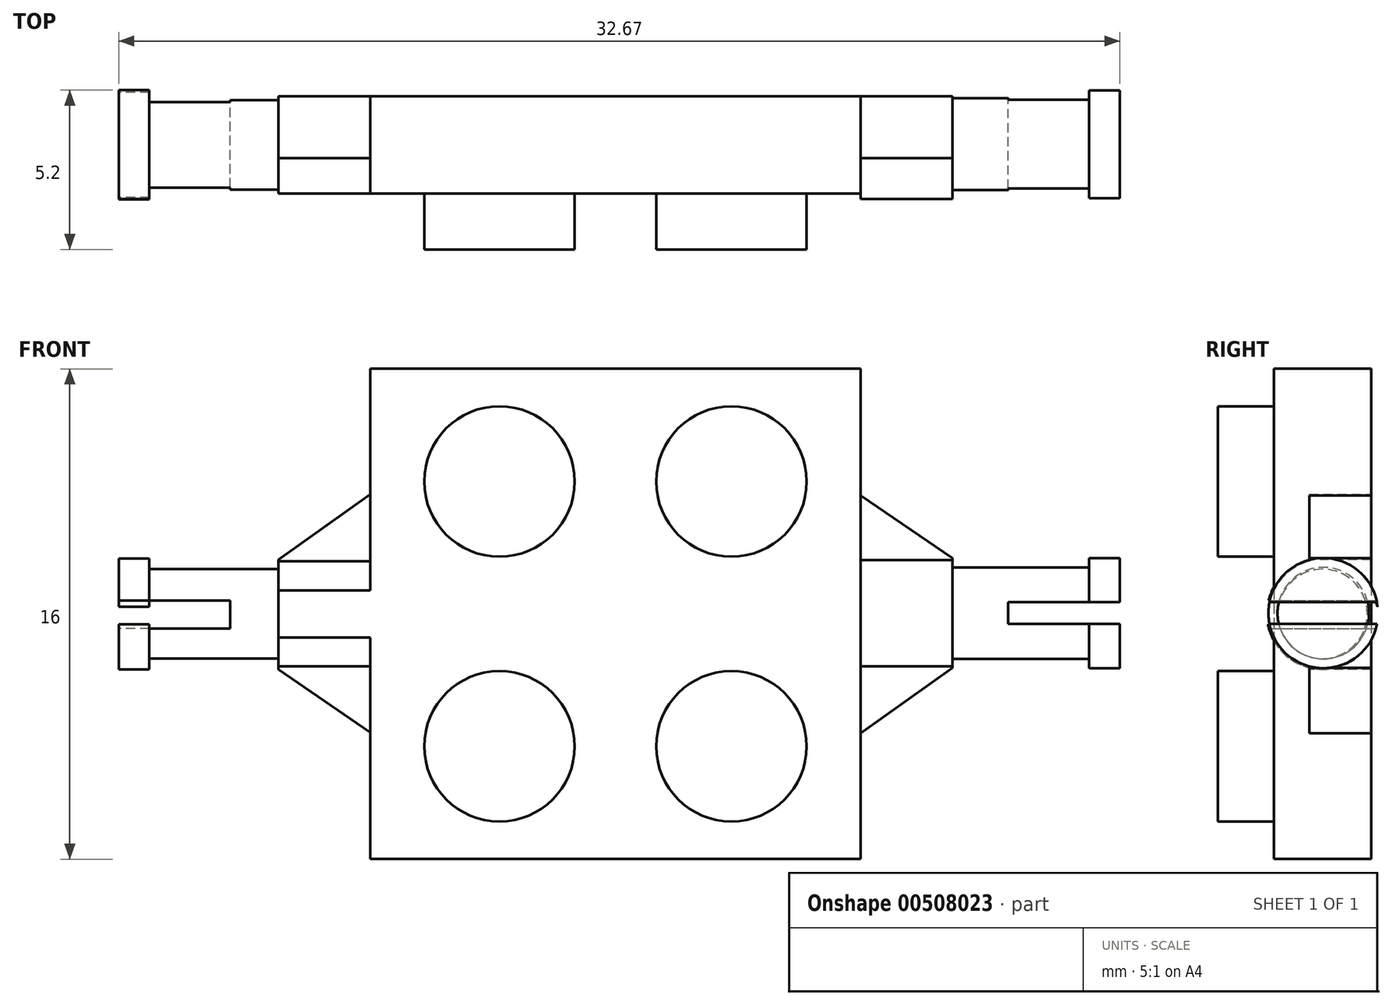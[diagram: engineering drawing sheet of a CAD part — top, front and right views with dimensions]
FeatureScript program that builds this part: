
annotation { "Feature Type Name" : "Feature", "Feature Type Description" : "" }
export const myFeature = defineFeature(function(context is Context, id is Id, definition is map)
    precondition{}
    {
        {
            var Q0;
            Q0=qCreatedBy(makeId("Front.planeOp"),FACE);
            var sketch = newSketch(context, id + "F0", { "sketchPlane" : qUnion([Q0])});
            skLineSegment(sketch, "E0.bottom", {"start": v(-45.17, 38.26) * mm, "end": v(-29.17, 38.26) * mm});
            skLineSegment(sketch, "E0.top", {"start": v(-45.17, 22.26) * mm, "end": v(-29.17, 22.26) * mm});
            skLineSegment(sketch, "E0.left", {"start": v(-45.17, 38.26) * mm, "end": v(-45.17, 22.26) * mm});
            skLineSegment(sketch, "E0.right", {"start": v(-29.17, 38.26) * mm, "end": v(-29.17, 22.26) * mm});
            skSolve(sketch);
        }
        {
            var Q0;
            Q0 = qSketchRegion(id + "F0", true);
            extrude(context, id + "F1", {"entities" : qUnion([Q0]), "depth" : 3.18 * mm});
        }
        {
            var Q0;
            Q0=makeQuery(id+"F1.opExtrude","CAP_FACE",FACE,{"disambiguationData":[OSD([sQuery(id+"F0.wireOp",EDGE,"E0.bottom"),sQuery(id+"F0.wireOp",EDGE,"E0.top"),sQuery(id+"F0.wireOp",EDGE,"E0.left"),sQuery(id+"F0.wireOp",EDGE,"E0.right")])],"isStart":false});
            var sketch = newSketch(context, id + "F2", { "sketchPlane" : qUnion([Q0])});
            skCircle(sketch, "E1", {"center": v(-40.96, 34.59) * mm, "radius": 2.46 * mm});
            skCircle(sketch, "E2", {"center": v(-33.39, 34.59) * mm, "radius": 2.46 * mm});
            skCircle(sketch, "E3", {"center": v(-33.39, 25.94) * mm, "radius": 2.46 * mm});
            skCircle(sketch, "E4", {"center": v(-40.96, 25.94) * mm, "radius": 2.46 * mm});
            skSolve(sketch);
        }
        {
            var Q0;
            Q0=makeQuery(id+"F2.imprint","IMPRINT",FACE,{"disambiguationData":[TD([[makeQuery(id+"F2.imprint","IMPRINT",EDGE,{"derivedFrom":sQuery(id+"F2.wireOp",EDGE,"E4")}),1.0]])]});
            var Q1;
            Q1=makeQuery(id+"F2.imprint","IMPRINT",FACE,{"disambiguationData":[TD([[makeQuery(id+"F2.imprint","IMPRINT",EDGE,{"derivedFrom":sQuery(id+"F2.wireOp",EDGE,"E3")}),1.0]])]});
            var Q2;
            Q2=makeQuery(id+"F2.imprint","IMPRINT",FACE,{"disambiguationData":[TD([[makeQuery(id+"F2.imprint","IMPRINT",EDGE,{"derivedFrom":sQuery(id+"F2.wireOp",EDGE,"E2")}),1.0]])]});
            var Q3;
            Q3=makeQuery(id+"F2.imprint","IMPRINT",FACE,{"disambiguationData":[TD([[makeQuery(id+"F2.imprint","IMPRINT",EDGE,{"derivedFrom":sQuery(id+"F2.wireOp",EDGE,"E1")}),1.0]])]});
            extrude(context, id + "F3", {"entities" : qUnion([Q0, Q1, Q2, Q3]), "operationType" : NewBodyOperationType.ADD, "depth" : 1.82 * mm});
        }
        {
            var Q0;
            Q0=makeQuery(id+"F1.opExtrude","SWEPT_FACE",FACE,{"disambiguationData":[OSD([sQuery(id+"F0.wireOp",EDGE,"E0.left")])]});
            var sketch = newSketch(context, id + "F4", { "sketchPlane" : qUnion([Q0])});
            skLineSegment(sketch, "E5.bottom", {"start": v(2.02, 34.16) * mm, "end": v(0, 34.16) * mm});
            skLineSegment(sketch, "E5.top", {"start": v(2.02, 26.4) * mm, "end": v(0, 26.4) * mm});
            skLineSegment(sketch, "E5.left", {"start": v(2.02, 34.16) * mm, "end": v(2.02, 26.4) * mm});
            skLineSegment(sketch, "E5.right", {"start": v(0, 34.16) * mm, "end": v(0, 26.4) * mm});
            skSolve(sketch);
        }
        {
            var Q0;
            Q0=makeQuery(id+"F4.imprint","IMPRINT",FACE,{"disambiguationData":[TD([[makeQuery(id+"F4.imprint","IMPRINT",EDGE,{"derivedFrom":sQuery(id+"F4.wireOp",EDGE,"E5.bottom")}),1.0]])]});
            extrude(context, id + "F5", {"entities" : qUnion([Q0]), "operationType" : NewBodyOperationType.ADD, "depth" : 3 * mm});
        }
        {
            var Q0;
            Q0=makeQuery(id+"F5.opExtrude","SWEPT_FACE",FACE,{"disambiguationData":[OSD([sQuery(id+"F4.wireOp",EDGE,"E5.left")])]});
            var sketch = newSketch(context, id + "F6", { "sketchPlane" : qUnion([Q0])});
            skLineSegment(sketch, "E6", {"start": v(-45.17, 26.4) * mm, "end": v(-48.17, 28.45) * mm});
            skLineSegment(sketch, "E7", {"start": v(-45.17, 34.16) * mm, "end": v(-48.17, 32.03) * mm});
            skLineSegment(sketch, "E8", {"start": v(-45.17, 34.16) * mm, "end": v(-48.17, 34.16) * mm});
            skLineSegment(sketch, "E9", {"start": v(-48.17, 34.16) * mm, "end": v(-48.17, 32.03) * mm});
            skLineSegment(sketch, "E10", {"start": v(-45.17, 26.4) * mm, "end": v(-48.17, 26.4) * mm});
            skLineSegment(sketch, "E11", {"start": v(-48.17, 26.4) * mm, "end": v(-48.17, 28.45) * mm});
            skSolve(sketch);
        }
        {
            var Q0;
            Q0=makeQuery(id+"F6.imprint","IMPRINT",FACE,{"disambiguationData":[TD([[makeQuery(id+"F6.imprint","IMPRINT",EDGE,{"derivedFrom":sQuery(id+"F6.wireOp",EDGE,"E7")}),-1.0]])]});
            var Q1;
            Q1=makeQuery(id+"F6.imprint","IMPRINT",FACE,{"disambiguationData":[TD([[makeQuery(id+"F6.imprint","IMPRINT",EDGE,{"derivedFrom":sQuery(id+"F6.wireOp",EDGE,"E6")}),1.0]])]});
            extrude(context, id + "F7", {"entities" : qUnion([Q0, Q1]), "operationType" : NewBodyOperationType.REMOVE, "oppositeDirection" : true, "depth" : 25 * mm});
        }
        {
            var Q0;
            Q0=makeQuery(id+"F1.opExtrude","SWEPT_FACE",FACE,{"disambiguationData":[OSD([sQuery(id+"F0.wireOp",EDGE,"E0.left")])]});
            var sketch = newSketch(context, id + "F8", { "sketchPlane" : qUnion([Q0])});
            skCircle(sketch, "E12", {"center": v(1.6, 30.26) * mm, "radius": 1.77 * mm});
            skPoint(sketch, "E12.centerSnap0", {"position": v(1.6, 38.26) * mm});
            skPoint(sketch, "E12.centerSnap1", {"position": v(3.18, 30.26) * mm});
            skSolve(sketch);
        }
        {
            var Q0;
            {var subQ0=sQuery(id+"F8.wireOp",EDGE,"E12");var subQ1=makeQuery(id+"F5.opExtrude","CAP_EDGE",EDGE,{"disambiguationData":[OSD([sQuery(id+"F4.wireOp",EDGE,"E5.left")])],"isStart":true});var subQ2=makeQuery(id+"F8.imprint","INTERSECT",VERTEX,{"disambiguationData":[OD(0.0)],"derivedFrom":[subQ1,subQ0]});Q0=makeQuery(id+"F8.imprint","IMPRINT",FACE,{"disambiguationData":[TD([[makeQuery(id+"F8.imprint","IMPRINT",EDGE,{"disambiguationData":[TD([[subQ2,1.0]])],"derivedFrom":subQ0}),1.0]])]});}
            var Q1;
            {var subQ0=sQuery(id+"F8.wireOp",EDGE,"E12");var subQ1=makeQuery(id+"F1.opExtrude","CAP_EDGE",EDGE,{"disambiguationData":[OSD([sQuery(id+"F0.wireOp",EDGE,"E0.left")])],"isStart":false});var subQ2=makeQuery(id+"F8.imprint","INTERSECT",VERTEX,{"disambiguationData":[OD(0.0)],"derivedFrom":[subQ1,subQ0]});Q1=makeQuery(id+"F8.imprint","IMPRINT",FACE,{"disambiguationData":[TD([[makeQuery(id+"F8.imprint","IMPRINT",EDGE,{"disambiguationData":[TD([[subQ2,1.0]])],"derivedFrom":subQ0}),1.0]])]});}
            extrude(context, id + "F9", {"entities" : qUnion([Q0, Q1]), "operationType" : NewBodyOperationType.ADD, "depth" : 3 * mm});
        }
        {
            var Q0;
            {var subQ0=sQuery(id+"F4.wireOp",EDGE,"E5.left");Q0=makeQuery(id+"F9.boolean.opBoolean","MERGE",FACE,{"derivedFrom":[makeQuery(id+"F5.opExtrude","CAP_FACE",FACE,{"disambiguationData":[OSD([sQuery(id+"F4.wireOp",EDGE,"E5.bottom"),sQuery(id+"F4.wireOp",EDGE,"E5.top"),subQ0,sQuery(id+"F4.wireOp",EDGE,"E5.right")])],"isStart":false}),makeQuery(id+"F9.opExtrude","CAP_FACE",FACE,{"disambiguationData":[OSD([subQ0,sQuery(id+"F8.wireOp",EDGE,"E12")])],"isStart":false})]});}
            var sketch = newSketch(context, id + "F10", { "sketchPlane" : qUnion([Q0])});
            skCircle(sketch, "E13", {"center": v(1.6, 30.26) * mm, "radius": 1.46 * mm});
            skSolve(sketch);
        }
        {
            var Q0;
            Q0=makeQuery(id+"F10.imprint","IMPRINT",FACE,{"disambiguationData":[TD([[makeQuery(id+"F10.imprint","IMPRINT",EDGE,{"derivedFrom":sQuery(id+"F10.wireOp",EDGE,"E13")}),1.0]])]});
            extrude(context, id + "F11", {"entities" : qUnion([Q0]), "operationType" : NewBodyOperationType.ADD, "depth" : 5.2 * mm});
        }
        {
            var Q0;
            Q0=makeQuery(id+"F11.opExtrude","CAP_FACE",FACE,{"disambiguationData":[OSD([sQuery(id+"F10.wireOp",EDGE,"E13")])],"isStart":false});
            var sketch = newSketch(context, id + "F12", { "sketchPlane" : qUnion([Q0])});
            skCircle(sketch, "E14", {"center": v(1.6, 30.26) * mm, "radius": 1.81 * mm});
            skSolve(sketch);
        }
        {
            var Q0;
            Q0=makeQuery(id+"F12.imprint","IMPRINT",FACE,{"disambiguationData":[TD([[makeQuery(id+"F12.imprint","IMPRINT",EDGE,{"derivedFrom":sQuery(id+"F12.wireOp",EDGE,"E14")}),1.0]])]});
            extrude(context, id + "F13", {"entities" : qUnion([Q0]), "operationType" : NewBodyOperationType.ADD, "oppositeDirection" : true, "depth" : 1 * mm});
        }
        {
            var Q0;
            {var subQ0=sQuery(id+"F10.wireOp",EDGE,"E13");Q0=makeQuery(id+"F13.boolean.opBoolean","MERGE",FACE,{"derivedFrom":[makeQuery(id+"F11.opExtrude","CAP_FACE",FACE,{"disambiguationData":[OSD([subQ0])],"isStart":false}),makeQuery(id+"F13.opExtrude","CAP_FACE",FACE,{"disambiguationData":[OSD([subQ0,sQuery(id+"F12.wireOp",EDGE,"E14")])],"isStart":true})]});}
            var sketch = newSketch(context, id + "F14", { "sketchPlane" : qUnion([Q0])});
            skLineSegment(sketch, "E15.bottom", {"start": v(3.35, 30.7) * mm, "end": v(-0.13, 30.7) * mm});
            skLineSegment(sketch, "E15.top", {"start": v(3.3, 29.78) * mm, "end": v(-0.16, 29.78) * mm});
            skArc(sketch, "E16", {"start": v(3.3, 29.78) * mm, "mid": v(3.43, 30.24) * mm, "end": v(3.35, 30.7) * mm});
            skArc(sketch, "E17", {"start": v(-0.13, 30.7) * mm, "mid": v(-0.25, 30.24) * mm, "end": v(-0.16, 29.78) * mm});
            skSolve(sketch);
        }
        {
            var Q0;
            {var subQ1=sQuery(id+"F14.wireOp",EDGE,"E15.bottom");Q0=makeQuery(id+"F14.imprint","IMPRINT",FACE,{"disambiguationData":[TD([[makeQuery(id+"F14.imprint","IMPRINT",EDGE,{"derivedFrom":subQ1}),1.0]])]});}
            extrude(context, id + "F15", {"entities" : qUnion([Q0]), "operationType" : NewBodyOperationType.REMOVE, "oppositeDirection" : true, "depth" : 3.64 * mm});
        }
        {
            var Q0;
            Q0=makeQuery(id+"F1.opExtrude","SWEPT_FACE",FACE,{"disambiguationData":[OSD([sQuery(id+"F0.wireOp",EDGE,"E0.right")])]});
            var sketch = newSketch(context, id + "F16", { "sketchPlane" : qUnion([Q0])});
            skLineSegment(sketch, "E18.bottom", {"start": v(-2.02, 26.36) * mm, "end": v(0, 26.36) * mm});
            skLineSegment(sketch, "E18.top", {"start": v(-2.02, 34.13) * mm, "end": v(0, 34.13) * mm});
            skLineSegment(sketch, "E18.left", {"start": v(-2.02, 26.36) * mm, "end": v(-2.02, 34.13) * mm});
            skLineSegment(sketch, "E18.right", {"start": v(0, 26.36) * mm, "end": v(0, 34.13) * mm});
            skSolve(sketch);
        }
        {
            var Q0;
            Q0=makeQuery(id+"F16.imprint","IMPRINT",FACE,{"disambiguationData":[TD([[makeQuery(id+"F16.imprint","IMPRINT",EDGE,{"derivedFrom":sQuery(id+"F16.wireOp",EDGE,"E18.bottom")}),1.0]])]});
            extrude(context, id + "F17", {"entities" : qUnion([Q0]), "operationType" : NewBodyOperationType.ADD, "depth" : 3 * mm});
        }
        {
            var Q0;
            Q0=makeQuery(id+"F17.opExtrude","SWEPT_FACE",FACE,{"disambiguationData":[OSD([sQuery(id+"F16.wireOp",EDGE,"E18.left")])]});
            var sketch = newSketch(context, id + "F18", { "sketchPlane" : qUnion([Q0])});
            skLineSegment(sketch, "E19", {"start": v(-29.17, 34.13) * mm, "end": v(-26.17, 32.08) * mm});
            skLineSegment(sketch, "E20", {"start": v(-26.17, 32.08) * mm, "end": v(-26.17, 34.13) * mm});
            skLineSegment(sketch, "E21", {"start": v(-26.17, 34.13) * mm, "end": v(-29.17, 34.13) * mm});
            skLineSegment(sketch, "E22", {"start": v(-29.17, 26.36) * mm, "end": v(-26.17, 28.5) * mm});
            skLineSegment(sketch, "E23", {"start": v(-26.17, 28.5) * mm, "end": v(-26.17, 26.36) * mm});
            skLineSegment(sketch, "E24", {"start": v(-26.17, 26.36) * mm, "end": v(-29.17, 26.36) * mm});
            skSolve(sketch);
        }
        {
            var Q0;
            Q0=makeQuery(id+"F18.imprint","IMPRINT",FACE,{"disambiguationData":[TD([[makeQuery(id+"F18.imprint","IMPRINT",EDGE,{"derivedFrom":sQuery(id+"F18.wireOp",EDGE,"E22")}),-1.0]])]});
            var Q1;
            Q1=makeQuery(id+"F18.imprint","IMPRINT",FACE,{"disambiguationData":[TD([[makeQuery(id+"F18.imprint","IMPRINT",EDGE,{"derivedFrom":sQuery(id+"F18.wireOp",EDGE,"E19")}),1.0]])]});
            extrude(context, id + "F19", {"entities" : qUnion([Q0, Q1]), "operationType" : NewBodyOperationType.REMOVE, "oppositeDirection" : true, "depth" : 25 * mm});
        }
        {
            var Q0;
            Q0=makeQuery(id+"F17.opExtrude","CAP_FACE",FACE,{"disambiguationData":[OSD([sQuery(id+"F16.wireOp",EDGE,"E18.bottom"),sQuery(id+"F16.wireOp",EDGE,"E18.top"),sQuery(id+"F16.wireOp",EDGE,"E18.left"),sQuery(id+"F16.wireOp",EDGE,"E18.right")])],"isStart":false});
            var sketch = newSketch(context, id + "F20", { "sketchPlane" : qUnion([Q0])});
            skCircle(sketch, "E25", {"center": v(-1.56, 30.3) * mm, "radius": 1.79 * mm});
            skPoint(sketch, "E25.centerSnap0", {"position": v(-2.02, 30.3) * mm});
            skSolve(sketch);
        }
        {
            var Q0;
            {var subQ0=sQuery(id+"F20.wireOp",EDGE,"E25");var subQ1=sQuery(id+"F16.wireOp",EDGE,"E18.left");var subQ6=makeQuery(id+"F17.opExtrude","CAP_EDGE",EDGE,{"disambiguationData":[OSD([subQ1])],"isStart":false});var subQ9=makeQuery(id+"F20.imprint","INTERSECT",VERTEX,{"disambiguationData":[OD(0.0)],"derivedFrom":[subQ6,subQ0]});Q0=makeQuery(id+"F20.imprint","IMPRINT",FACE,{"disambiguationData":[TD([[makeQuery(id+"F20.imprint","IMPRINT",EDGE,{"disambiguationData":[TD([[subQ9,1.0]])],"derivedFrom":subQ6}),-1.0]])]});}
            var Q1;
            {var subQ0=sQuery(id+"F20.wireOp",EDGE,"E25");var subQ1=makeQuery(id+"F17.opExtrude","CAP_EDGE",EDGE,{"disambiguationData":[OSD([sQuery(id+"F16.wireOp",EDGE,"E18.left")])],"isStart":false});var subQ2=makeQuery(id+"F20.imprint","INTERSECT",VERTEX,{"disambiguationData":[OD(0.0)],"derivedFrom":[subQ1,subQ0]});Q1=makeQuery(id+"F20.imprint","IMPRINT",FACE,{"disambiguationData":[TD([[makeQuery(id+"F20.imprint","IMPRINT",EDGE,{"disambiguationData":[TD([[subQ2,-1.0]])],"derivedFrom":subQ0}),1.0]])]});}
            var Q2;
            {var subQ0=sQuery(id+"F20.wireOp",EDGE,"E25");var subQ1=makeQuery(id+"F17.opExtrude","CAP_EDGE",EDGE,{"disambiguationData":[OSD([sQuery(id+"F16.wireOp",EDGE,"E18.right")])],"isStart":false});var subQ2=makeQuery(id+"F20.imprint","INTERSECT",VERTEX,{"disambiguationData":[OD(0.0)],"derivedFrom":[subQ1,subQ0]});Q2=makeQuery(id+"F20.imprint","IMPRINT",FACE,{"disambiguationData":[TD([[makeQuery(id+"F20.imprint","IMPRINT",EDGE,{"disambiguationData":[TD([[subQ2,1.0]])],"derivedFrom":subQ0}),1.0]])]});}
            extrude(context, id + "F21", {"entities" : qUnion([Q0, Q1, Q2]), "operationType" : NewBodyOperationType.ADD, "oppositeDirection" : true, "depth" : 3 * mm});
        }
        {
            var Q0;
            Q0=makeQuery(id+"F21.boolean.opBoolean","MERGE",FACE,{"derivedFrom":[makeQuery(id+"F17.opExtrude","CAP_FACE",FACE,{"disambiguationData":[OSD([sQuery(id+"F16.wireOp",EDGE,"E18.bottom"),sQuery(id+"F16.wireOp",EDGE,"E18.top"),sQuery(id+"F16.wireOp",EDGE,"E18.left"),sQuery(id+"F16.wireOp",EDGE,"E18.right")])],"isStart":false}),makeQuery(id+"F21.opExtrude","CAP_FACE",FACE,{"disambiguationData":[OSD([sQuery(id+"F20.wireOp",EDGE,"E25")])],"isStart":true})]});
            var sketch = newSketch(context, id + "F22", { "sketchPlane" : qUnion([Q0])});
            skCircle(sketch, "E26", {"center": v(-1.56, 30.3) * mm, "radius": 1.5 * mm});
            skSolve(sketch);
        }
        {
            var Q0;
            Q0=makeQuery(id+"F22.imprint","IMPRINT",FACE,{"disambiguationData":[TD([[makeQuery(id+"F22.imprint","IMPRINT",EDGE,{"derivedFrom":sQuery(id+"F22.wireOp",EDGE,"E26")}),1.0]])]});
            extrude(context, id + "F23", {"entities" : qUnion([Q0]), "operationType" : NewBodyOperationType.ADD, "depth" : 5.46 * mm});
        }
        {
            var Q0;
            Q0=makeQuery(id+"F23.opExtrude","CAP_FACE",FACE,{"disambiguationData":[OSD([sQuery(id+"F22.wireOp",EDGE,"E26")])],"isStart":false});
            var sketch = newSketch(context, id + "F24", { "sketchPlane" : qUnion([Q0])});
            skCircle(sketch, "E27", {"center": v(-1.56, 30.3) * mm, "radius": 1.8 * mm});
            skSolve(sketch);
        }
        {
            var Q0;
            Q0 = qSketchRegion(id + "F24", true);
            extrude(context, id + "F25", {"entities" : qUnion([Q0]), "operationType" : NewBodyOperationType.ADD, "oppositeDirection" : true, "depth" : 1 * mm});
        }
        {
            var Q0;
            Q0=makeQuery(id+"F25.boolean.opBoolean","MERGE",FACE,{"derivedFrom":[makeQuery(id+"F23.opExtrude","CAP_FACE",FACE,{"disambiguationData":[OSD([sQuery(id+"F22.wireOp",EDGE,"E26")])],"isStart":false}),makeQuery(id+"F25.opExtrude","CAP_FACE",FACE,{"disambiguationData":[OSD([sQuery(id+"F24.wireOp",EDGE,"E27")])],"isStart":true})]});
            var sketch = newSketch(context, id + "F26", { "sketchPlane" : qUnion([Q0])});
            skLineSegment(sketch, "E28.bottom", {"start": v(-3.32, 29.94) * mm, "end": v(0.2, 29.94) * mm});
            skLineSegment(sketch, "E28.top", {"start": v(-3.32, 30.65) * mm, "end": v(0.2, 30.65) * mm});
            skArc(sketch, "E29", {"start": v(-3.32, 30.65) * mm, "mid": v(-3.38, 30.3) * mm, "end": v(-3.32, 29.94) * mm});
            skArc(sketch, "E30", {"start": v(0.2, 29.94) * mm, "mid": v(0.25, 30.3) * mm, "end": v(0.2, 30.65) * mm});
            skSolve(sketch);
        }
        {
            var Q0;
            Q0 = qSketchRegion(id + "F26", true);
            extrude(context, id + "F27", {"entities" : qUnion([Q0]), "operationType" : NewBodyOperationType.REMOVE, "oppositeDirection" : true, "depth" : 3.64 * mm});
        }
    });
